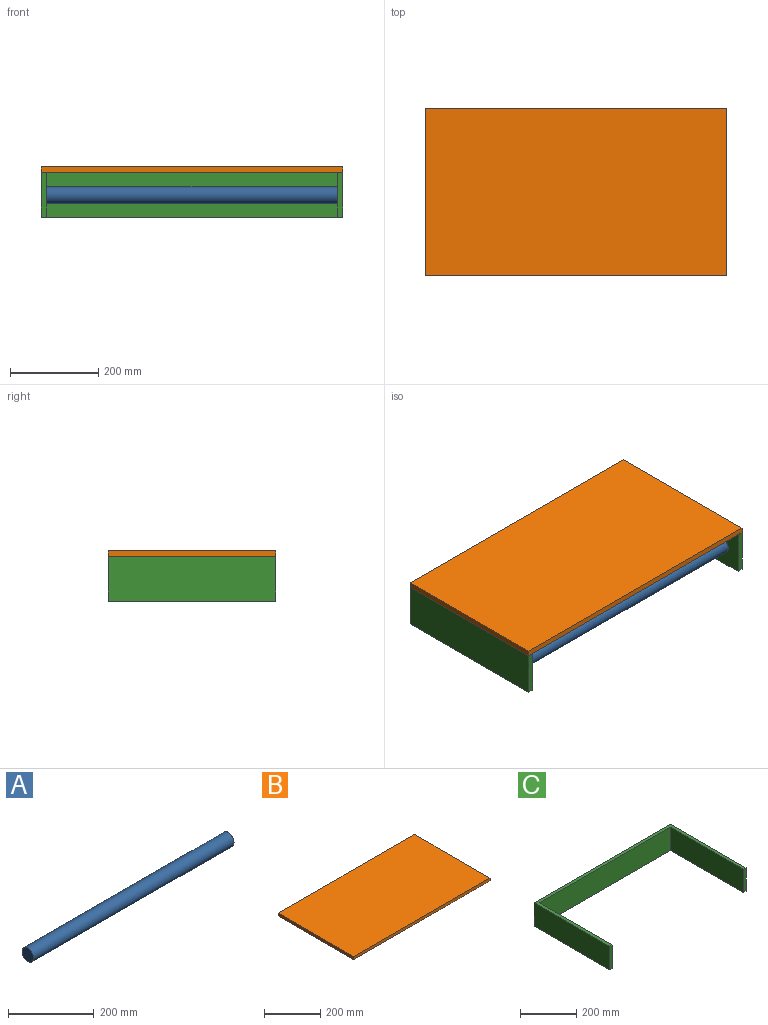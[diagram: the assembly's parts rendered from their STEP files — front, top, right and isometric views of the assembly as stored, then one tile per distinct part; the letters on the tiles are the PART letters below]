
ASSEMBLY  parts=3 mates=4
PART A: 3 faces, bbox 660.4x38.1x38.1 mm
  f0: cylinder r=19.05mm len=660.4mm, axis (-1,0,0), area 79046.4mm2, adj f1,f2
  f1: plane 38.1x38.1mm, normal (1,0,0), area 1140.1mm2, adj f0
  f2: plane 38.1x38.1mm, normal (-1,0,0), area 1140.1mm2, adj f0
PART B: 6 faces, bbox 685.8x381x12.7 mm
  f0: plane 381x12.7mm, normal (-1,0,0), area 4838.7mm2, adj f1,f3,f4,f5
  f1: plane 685.8x12.7mm, normal (0,-1,0), area 8709.7mm2, adj f0,f2,f4,f5
  f2: plane 381x12.7mm, normal (1,0,0), area 4838.7mm2, adj f1,f3,f4,f5
  f3: plane 685.8x12.7mm, normal (0,1,0), area 8709.7mm2, adj f0,f2,f4,f5
  f4: plane 685.8x381mm, normal (0,0,1), area 261289.8mm2, adj f0,f1,f2,f3
  f5: plane 685.8x381mm, normal (0,0,-1), area 261289.8mm2, adj f0,f1,f2,f3
PART C: 10 faces, bbox 685.8x381x101.6 mm
  f0: plane 381x101.6mm, normal (-1,0,0), area 38709.6mm2, adj f1,f7,f8,f9
  f1: plane 101.6x12.7mm, normal (0,-1,0), area 1290.3mm2, adj f0,f2,f8,f9
  f2: plane 368.3x101.6mm, normal (1,0,0), area 37419.3mm2, adj f1,f3,f8,f9
  f3: plane 660.4x101.6mm, normal (0,-1,0), area 67096.6mm2, adj f2,f4,f8,f9
  f4: plane 368.3x101.6mm, normal (-1,0,0), area 37419.3mm2, adj f3,f5,f8,f9
  f5: plane 101.6x12.7mm, normal (0,-1,0), area 1290.3mm2, adj f4,f6,f8,f9
  f6: plane 381x101.6mm, normal (1,0,0), area 38709.6mm2, adj f5,f7,f8,f9
  f7: plane 685.8x101.6mm, normal (0,1,0), area 69677.3mm2, adj f0,f6,f8,f9
  f8: plane 685.8x381mm, normal (0,0,-1), area 18064.5mm2, adj f0,f1,f2,f3,f4,f5,f6,f7
  f9: plane 685.8x381mm, normal (0,0,1), area 18064.5mm2, adj f0,f1,f2,f3,f4,f5,f6,f7
PLACE A t=(-170.46,-38.82,-97.92)mm
PLACE B t=(-183.16,-89.54,-46.11)mm
PLACE C t=(-183.16,-89.54,-46.11)mm
MATE planar B.f1 <-> C.f1  axis (0,-1,0) through (159.74,-89.54,-39.76)mm
MATE planar B.f2 <-> C.f6  axis (1,0,0) through (502.64,100.96,-39.76)mm
MATE planar A.f0 <-> C.f4  axis (1,0,0) through (489.94,-38.82,-97.92)mm
MATE planar B.f5 <-> C.f9  axis (0,0,-1) through (159.74,100.96,-46.11)mm
